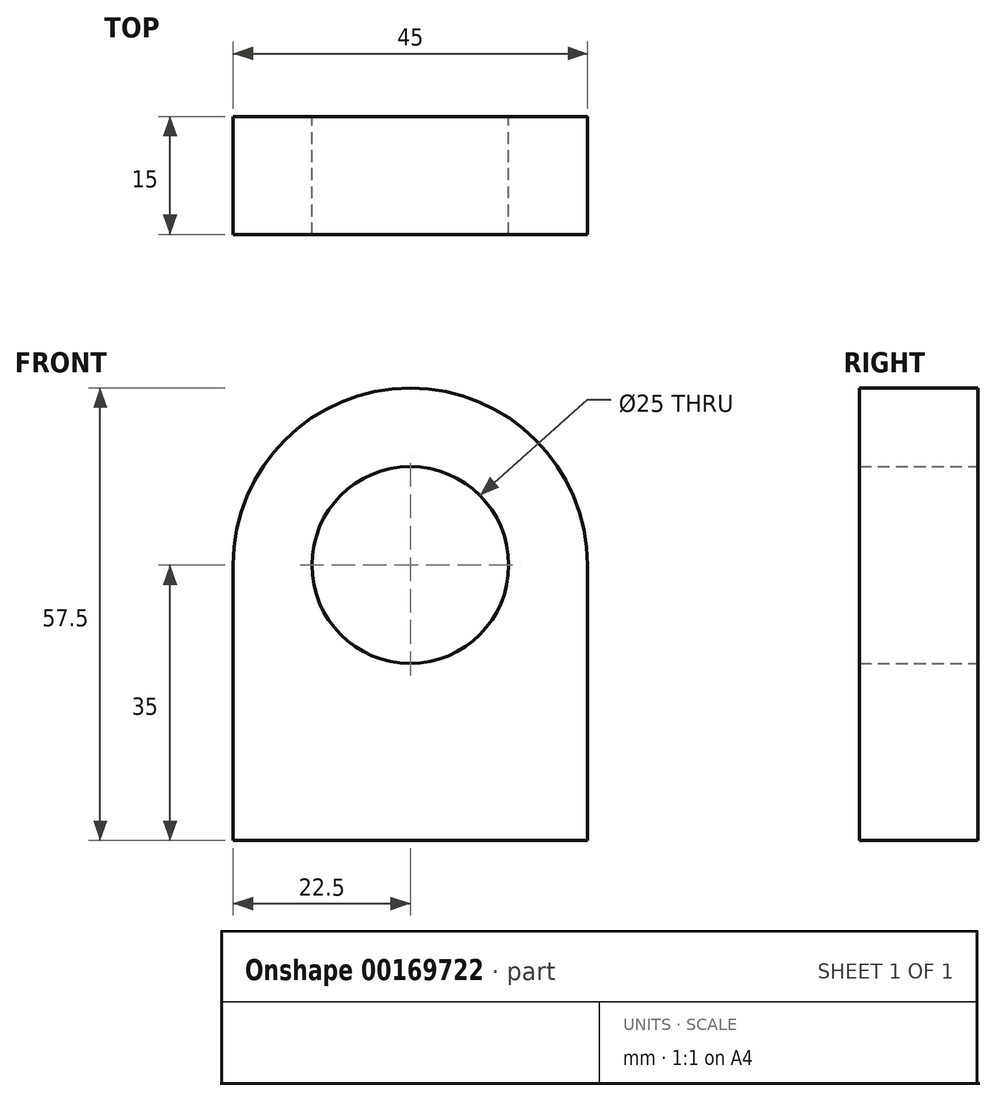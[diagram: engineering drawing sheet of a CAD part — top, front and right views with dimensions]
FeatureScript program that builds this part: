
annotation { "Feature Type Name" : "Feature", "Feature Type Description" : "" }
export const myFeature = defineFeature(function(context is Context, id is Id, definition is map)
    precondition{}
    {
        {
            var Q0;
            Q0=qCreatedBy(makeId("Front.planeOp"),FACE);
            var sketch = newSketch(context, id + "F0", { "sketchPlane" : qUnion([Q0])});
            skLineSegment(sketch, "E0.bottom", {"start": v(0, 0) * mm, "end": v(45, 0) * mm});
            skLineSegment(sketch, "E0.top", {"start": v(0, 35) * mm, "end": v(45, 35) * mm});
            skLineSegment(sketch, "E0.left", {"start": v(0, 0) * mm, "end": v(0, 35) * mm});
            skLineSegment(sketch, "E0.right", {"start": v(45, 0) * mm, "end": v(45, 35) * mm});
            skArc(sketch, "E1", {"start": v(45, 35) * mm, "mid": v(22.5, 57.5) * mm, "end": v(0, 35) * mm});
            skCircle(sketch, "E2", {"center": v(22.5, 35) * mm, "radius": 12.5 * mm});
            skSolve(sketch);
        }
        {
            var Q0;
            Q0=qSketchRegion(id+"F0",true);
            extrude(context, id + "F1", {"entities" : qUnion([Q0]), "depth" : 15 * mm});
        }
    });
